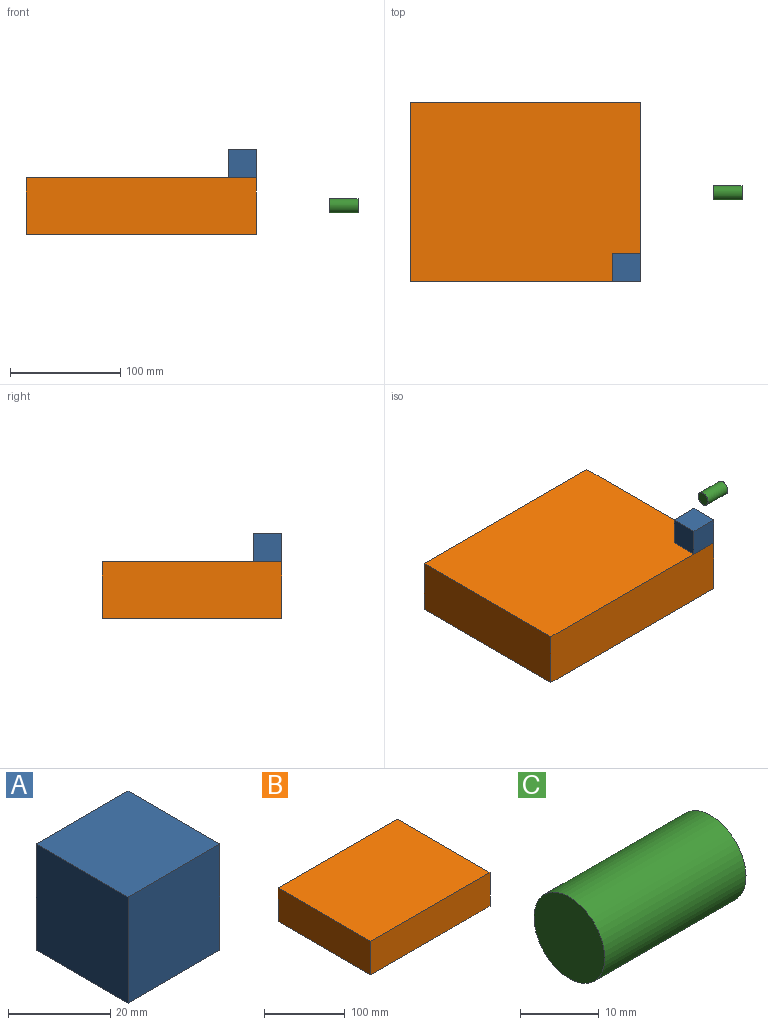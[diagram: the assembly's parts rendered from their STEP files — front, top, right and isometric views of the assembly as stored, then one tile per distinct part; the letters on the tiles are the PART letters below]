
ASSEMBLY  parts=3 mates=2
PART A: 6 faces, bbox 25.4x25.4x25.4 mm
  f0: plane 25.4x25.4mm, normal (0,1,0), area 645.2mm2, adj f1,f3,f4,f5
  f1: plane 25.4x25.4mm, normal (-1,0,0), area 645.2mm2, adj f0,f2,f4,f5
  f2: plane 25.4x25.4mm, normal (0,-1,0), area 645.2mm2, adj f1,f3,f4,f5
  f3: plane 25.4x25.4mm, normal (1,0,0), area 645.2mm2, adj f0,f2,f4,f5
  f4: plane 25.4x25.4mm, normal (0,0,1), area 645.2mm2, adj f0,f1,f2,f3
  f5: plane 25.4x25.4mm, normal (0,0,-1), area 645.2mm2, adj f0,f1,f2,f3
PART B: 8 faces, bbox 208.6x162.5x50.8 mm
  f0: plane 208.58x50.8mm, normal (0,1,0), area 10595.6mm2, adj f1,f3,f4,f5
  f1: plane 162.51x50.8mm, normal (-1,0,0), area 8255.3mm2, adj f0,f2,f4,f5
  f2: plane 208.58x50.8mm, normal (0,-1,0), area 10595.6mm2, adj f1,f3,f4,f5
  f3: plane 162.51x50.8mm, normal (1,0,0), area 7576.2mm2, adj f0,f2,f4,f5,f6
  f4: plane 208.58x162.51mm, normal (0,0,1), area 33894.6mm2, adj f0,f1,f2,f3
  f5: plane 208.58x162.51mm, normal (0,0,-1), area 33894.6mm2, adj f0,f1,f2,f3
  f6: cylinder r=14.7mm len=29.4mm, axis (1,0,0), area 2346.3mm2, adj f3,f7
  f7: plane 29.4x29.4mm, normal (1,0,0), area 679.1mm2, adj f6
PART C: 3 faces, bbox 25.4x12.7x12.7 mm
  f0: cylinder r=6.35mm len=25.4mm, axis (-1,0,0), area 1013.4mm2, adj f1,f2
  f1: plane 12.7x12.7mm, normal (1,0,0), area 126.7mm2, adj f0
  f2: plane 12.7x12.7mm, normal (-1,0,0), area 126.7mm2, adj f0
PLACE A t=(-92.72,-51.16,-18.05)mm
PLACE B t=(-170.31,-7.59,-68.85)mm
PLACE C t=(6.64,-9.56,-43.18)mm
MATE fastened A.f5 <-> B.f4  axis (0,0,1) through (-60.19,-90.09,-18.05)mm
MATE slider B.f3 <-> C.f0  axis (1,0,0) through (-60.19,-9.56,-43.18)mm
